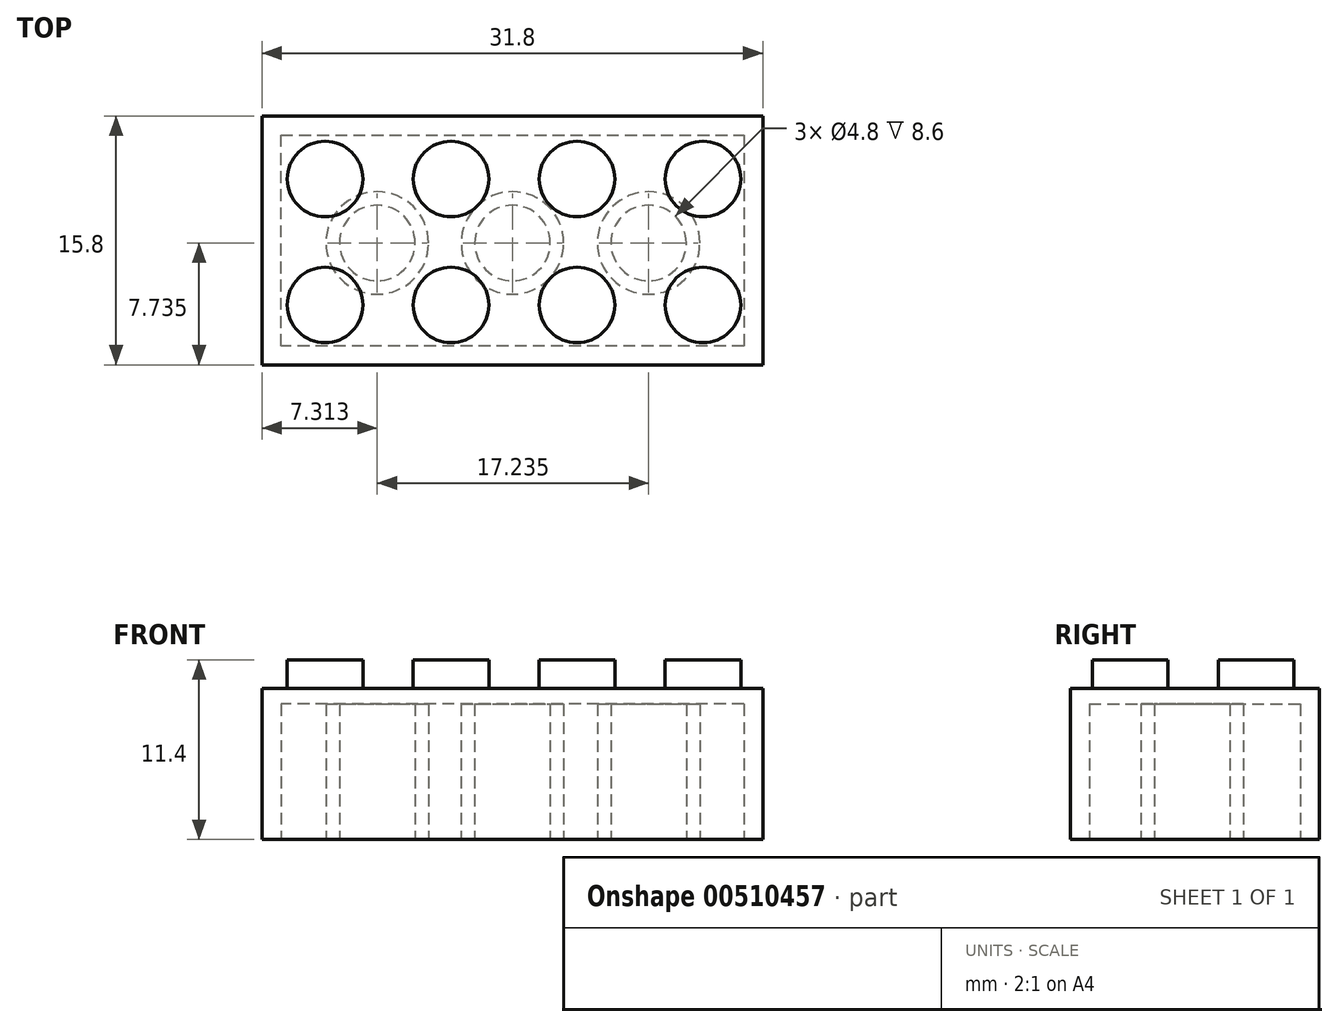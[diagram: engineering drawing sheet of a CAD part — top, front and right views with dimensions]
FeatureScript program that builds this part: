
annotation { "Feature Type Name" : "Feature", "Feature Type Description" : "" }
export const myFeature = defineFeature(function(context is Context, id is Id, definition is map)
    precondition{}
    {
        {
            var Q0;
            Q0=qCreatedBy(makeId("Top.planeOp"),FACE);
            var sketch = newSketch(context, id + "F0", { "sketchPlane" : qUnion([Q0])});
            skLineSegment(sketch, "E0.bottom", {"start": v(0, 0) * mm, "end": v(31.8, 0) * mm});
            skLineSegment(sketch, "E0.top", {"start": v(0, -15.8) * mm, "end": v(31.8, -15.8) * mm});
            skLineSegment(sketch, "E0.left", {"start": v(0, 0) * mm, "end": v(0, -15.8) * mm});
            skLineSegment(sketch, "E0.right", {"start": v(31.8, 0) * mm, "end": v(31.8, -15.8) * mm});
            skSolve(sketch);
        }
        {
            var Q0;
            Q0 = qSketchRegion(id + "F0", true);
            extrude(context, id + "F1", {"entities" : qUnion([Q0]), "oppositeDirection" : true, "depth" : 9.6 * mm});
        }
        {
            var Q0;
            Q0=qCreatedBy(makeId("Top.planeOp"),FACE);
            var sketch = newSketch(context, id + "F2", { "sketchPlane" : qUnion([Q0])});
            skLineSegment(sketch, "E1", {"start": v(4, 0) * mm, "end": v(4, -8) * mm, "construction": true});
            skLineSegment(sketch, "E2", {"start": v(0, -4) * mm, "end": v(8, -4) * mm, "construction": true});
            skLineSegment(sketch, "E3", {"start": v(4, -4) * mm, "end": v(12, -4) * mm, "construction": true});
            skLineSegment(sketch, "E4", {"start": v(12, -4) * mm, "end": v(20, -4) * mm, "construction": true});
            skLineSegment(sketch, "E5", {"start": v(20, -4) * mm, "end": v(28, -4) * mm, "construction": true});
            skLineSegment(sketch, "E6", {"start": v(28, -4) * mm, "end": v(28, -12) * mm, "construction": true});
            skLineSegment(sketch, "E7", {"start": v(28, -12) * mm, "end": v(20, -12) * mm, "construction": true});
            skLineSegment(sketch, "E8", {"start": v(20, -12) * mm, "end": v(12, -12) * mm, "construction": true});
            skLineSegment(sketch, "E9", {"start": v(12, -12) * mm, "end": v(4, -12) * mm, "construction": true});
            skLineSegment(sketch, "E10", {"start": v(4, -12) * mm, "end": v(4, -4) * mm, "construction": true});
            skCircle(sketch, "E11", {"center": v(4, -4) * mm, "radius": 2.4 * mm});
            skCircle(sketch, "E12", {"center": v(12, -4) * mm, "radius": 2.4 * mm});
            skCircle(sketch, "E13", {"center": v(20, -4) * mm, "radius": 2.4 * mm});
            skCircle(sketch, "E14", {"center": v(28, -4) * mm, "radius": 2.4 * mm});
            skCircle(sketch, "E15", {"center": v(28, -12) * mm, "radius": 2.4 * mm});
            skCircle(sketch, "E16", {"center": v(20, -12) * mm, "radius": 2.4 * mm});
            skCircle(sketch, "E17", {"center": v(12, -12) * mm, "radius": 2.4 * mm});
            skCircle(sketch, "E18", {"center": v(4, -12) * mm, "radius": 2.4 * mm});
            skSolve(sketch);
        }
        {
            var Q0;
            Q0 = qSketchRegion(id + "F2", true);
            extrude(context, id + "F3", {"entities" : qUnion([Q0]), "operationType" : NewBodyOperationType.ADD, "depth" : 1.8 * mm, "offsetDistance" : 25.4 * mm});
        }
        {
            var Q0;
            Q0=makeQuery(id+"F1.opExtrude","CAP_FACE",FACE,{"disambiguationData":[OSD([sQuery(id+"F0.wireOp",EDGE,"E0.bottom"),sQuery(id+"F0.wireOp",EDGE,"E0.top"),sQuery(id+"F0.wireOp",EDGE,"E0.left"),sQuery(id+"F0.wireOp",EDGE,"E0.right")])],"isStart":false});
            var sketch = newSketch(context, id + "F4", { "sketchPlane" : qUnion([Q0])});
            skCircle(sketch, "E19", {"center": v(7.31, 8.06) * mm, "radius": 2.4 * mm});
            skCircle(sketch, "E20", {"center": v(7.31, 8.06) * mm, "radius": 3.25 * mm});
            skCircle(sketch, "E21", {"center": v(15.9, 8.06) * mm, "radius": 2.4 * mm});
            skCircle(sketch, "E22", {"center": v(15.9, 8.06) * mm, "radius": 3.25 * mm});
            skCircle(sketch, "E23", {"center": v(24.55, 8.06) * mm, "radius": 2.4 * mm});
            skCircle(sketch, "E24", {"center": v(24.55, 8.06) * mm, "radius": 3.25 * mm});
            skLineSegment(sketch, "E25", {"start": v(7.31, 8.06) * mm, "end": v(15.9, 8.06) * mm, "construction": true});
            skLineSegment(sketch, "E26", {"start": v(15.9, 8.06) * mm, "end": v(24.55, 8.06) * mm, "construction": true});
            skLineSegment(sketch, "E27", {"start": v(15.9, 15.8) * mm, "end": v(15.9, 8.06) * mm, "construction": true});
            skLineSegment(sketch, "E28", {"start": v(1.2, 14.6) * mm, "end": v(1.2, 1.2) * mm});
            skLineSegment(sketch, "E29", {"start": v(1.2, 1.2) * mm, "end": v(30.6, 1.2) * mm});
            skLineSegment(sketch, "E30", {"start": v(30.6, 1.2) * mm, "end": v(30.6, 14.6) * mm});
            skLineSegment(sketch, "E31", {"start": v(30.6, 14.6) * mm, "end": v(1.2, 14.6) * mm});
            skSolve(sketch);
        }
        {
            var Q0;
            Q0 = qSketchRegion(id + "F4", true);
            var Q1;
            Q1=makeQuery(id+"F4.imprint","IMPRINT",FACE,{"disambiguationData":[TD([[makeQuery(id+"F4.imprint","IMPRINT",EDGE,{"derivedFrom":sQuery(id+"F4.wireOp",EDGE,"E19")}),1.0]])]});
            var Q2;
            Q2=makeQuery(id+"F4.imprint","IMPRINT",FACE,{"disambiguationData":[TD([[makeQuery(id+"F4.imprint","IMPRINT",EDGE,{"derivedFrom":sQuery(id+"F4.wireOp",EDGE,"E21")}),1.0]])]});
            var Q3;
            Q3=makeQuery(id+"F4.imprint","IMPRINT",FACE,{"disambiguationData":[TD([[makeQuery(id+"F4.imprint","IMPRINT",EDGE,{"derivedFrom":sQuery(id+"F4.wireOp",EDGE,"E23")}),1.0]])]});
            extrude(context, id + "F5", {"entities" : qUnion([Q0, Q1, Q2, Q3]), "operationType" : NewBodyOperationType.REMOVE, "oppositeDirection" : true, "depth" : 8.6 * mm, "offsetDistance" : 25.4 * mm});
        }
    });
